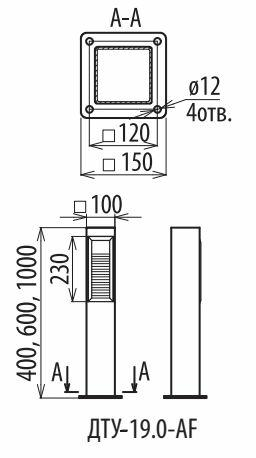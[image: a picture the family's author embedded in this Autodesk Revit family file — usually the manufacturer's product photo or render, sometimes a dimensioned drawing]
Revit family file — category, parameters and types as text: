
# Revit family: svetilnik_alfresco_slim
name_source: partatom
category: Осветительные приборы
revit_build: Autodesk Revit 2016 (Build: 20150506_1715(x64)
units: mm (PartAtom-declared; Revit-internal decimal feet)

## family parameters
Всегда вертикально = Да
Источник света = Да
На основе рабочей плоскости = Нет
Общий = Нет
При загрузке вырезать с полостями = Нет
Размер круглого соединителя = Использовать диаметр
Тип детали = Нормальный
Точка расчета площади = Нет

## types (4) — shared parameters
ADSK_Единица измерения = шт.
ADSK_Завод-изготовитель = ALFRESCO
ADSK_Количество фаз = 2
ADSK_Количество фаз числовое = 2
ADSK_Коэффициент мощности = 0.98
ADSK_Модель = ДТУ-21-AF Слим
ADSK_Напряжение = 220 В
ADSK_Ток = 0 А
ADSK_Энергоэффективность = 110 лм/Вт
IP Class = IP 66
URL = http://www.allfresco.ru
Блок аварийного питания = Нет
Видимая форма излучения при визуализации = Нет
Высота плафона = 100 мм
Изготовитель = ALFRESCO
Излучение по диаметру окружности = 100 мм
Класс защиты = 1
Класс пожароопасности = F (светильники предназначены для установки непосредственно на поверхность из нормально воспламеняемых материалов)
Климатическая зона = У1
Корпус светильника = Сталь крашенная чёрная
Материал рассеивателя = PC
Область использования = ландшафт, коттедж. Посёлки,микрорайоны
Плафон = PC
Радиус  корпуса светильника = 54 мм
Радиус фланца = 95 мм
Светофильтр = 16777215
Смещение цветовой температуры при затухании лампы = <Нет>
Температура эксплуатации = -35 +40
Тип ИС = LED-светодиоды
Тип КСС = Круглосимметричная
Тип ПРА = -
Тип продукции = LED-светильник
Угол наклона = 90.00°
Цветовая температура = 2700-6500

## per-type parameters (varying)
| type | ADSK_Артикул | ADSK_Масса | ADSK_Наименование | ADSK_Номинальная мощность | ADSK_Полная мощность | ADSK_Размер_Высота | Высота крышки | Полная установленная мощность | Файл фотометрической сетки |
| Слим-0.5 (1) | ДТУ2112 | 5.2 | Светодиодный светильник Слим ДТУ-21-AF-4Вт-0,5-IP66 | 4 Вт | 4 В·А | 500 мм | 85 мм | 4 В·А | Slim 4W.ies |
| Слим-0.5 (2) | ДТУ2110 | 5.5 | Светодиодный светильник Слим ДТУ-21-AF-12Вт-0,5-IP66 | 12 Вт | 12 В·А | 500 мм | 85 мм | 12 В·А | Slim12W.ies |
| Слим-1.0 (1) | ДТУ2113 | 9.3 | Светодиодный светильник Слим ДТУ-21-AF-4Вт-1,0-IP66 | 4 Вт | 4 В·А | 1000 мм | 50 мм | 4 В·А | Slim 4W.ies |
| Слим-1.0 (2) | ДТУ2111 | 9.8 | Светодиодный светильник Слим ДТУ-21-AF-12Вт-1,0-IP66 | 12 Вт | 12 В·А | 1000 мм | 50 мм | 12 В·А | Slim12W.ies |

## geometry (parser evidence)
native form markers: Blend x2
no freeform markers — native parametric forms only
